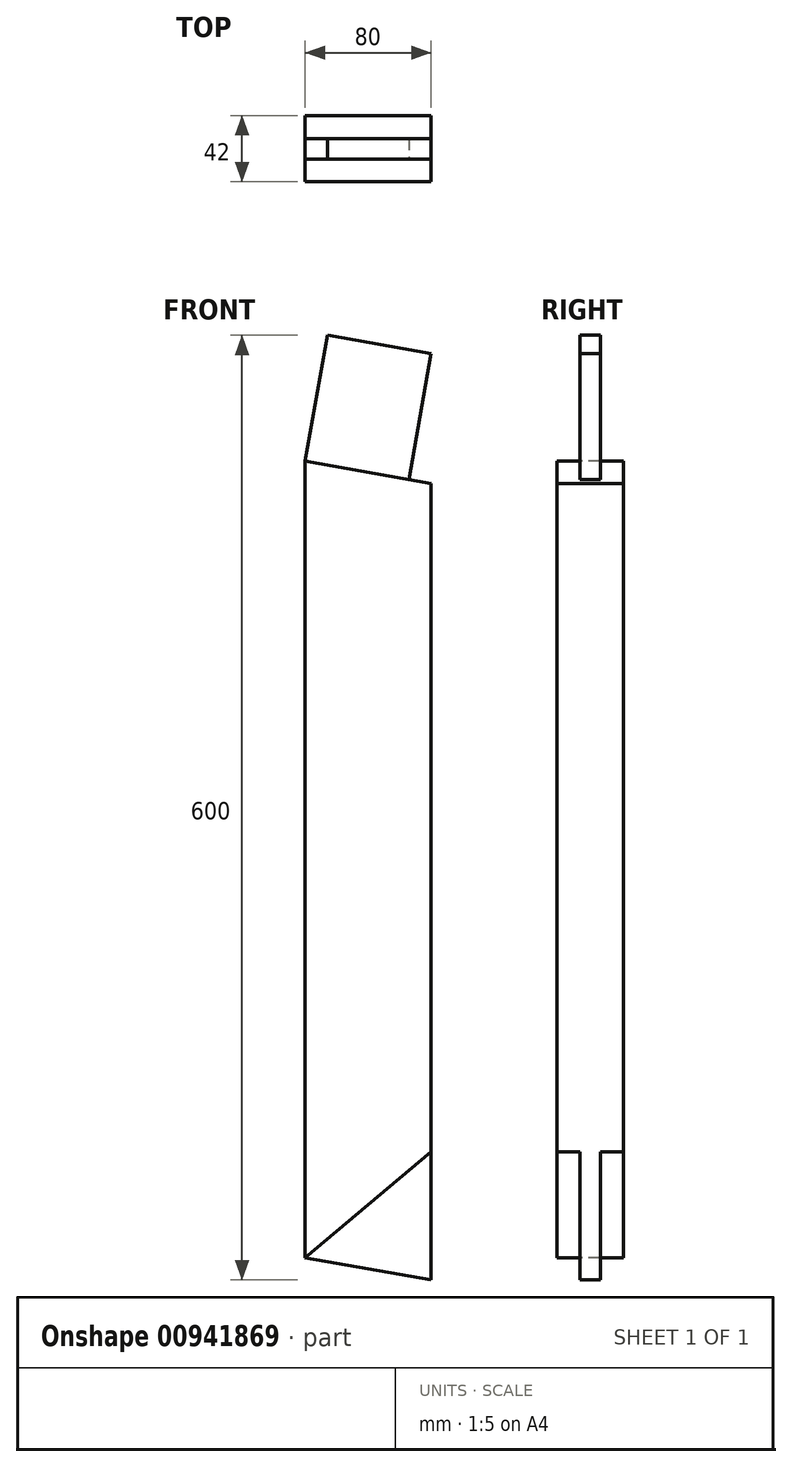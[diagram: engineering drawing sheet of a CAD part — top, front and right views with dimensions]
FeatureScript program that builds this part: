
annotation { "Feature Type Name" : "Feature", "Feature Type Description" : "" }
export const myFeature = defineFeature(function(context is Context, id is Id, definition is map)
    precondition{}
    {
        {
            var Q0;
            Q0=qCreatedBy(makeId("Front.planeOp"),FACE);
            var sketch = newSketch(context, id + "F0", { "sketchPlane" : qUnion([Q0])});
            skLineSegment(sketch, "E0.bottom", {"start": v(40, -300) * mm, "end": v(-40, -300) * mm});
            skLineSegment(sketch, "E0.top", {"start": v(40, 300) * mm, "end": v(-40, 300) * mm});
            skLineSegment(sketch, "E0.left", {"start": v(40, -300) * mm, "end": v(40, 300) * mm});
            skLineSegment(sketch, "E0.right", {"start": v(-40, -300) * mm, "end": v(-40, 300) * mm});
            skPoint(sketch, "E0.middle", {"position": v(0, 0) * mm});
            skSolve(sketch);
        }
        {
            var Q0;
            Q0=makeQuery(id+"F0.imprint","IMPRINT",FACE,{"disambiguationData":[TD([[makeQuery(id+"F0.imprint","IMPRINT",EDGE,{"derivedFrom":sQuery(id+"F0.wireOp",EDGE,"E0.bottom")}),-1.0]])]});
            extrude(context, id + "F1", {"entities" : qUnion([Q0]), "depth" : 42 * mm, "offsetDistance" : 25 * mm});
        }
        {
            var Q0;
            Q0=makeQuery(id+"F1.opExtrude","CAP_FACE",FACE,{"disambiguationData":[OSD([sQuery(id+"F0.wireOp",EDGE,"E0.bottom"),sQuery(id+"F0.wireOp",EDGE,"E0.top"),sQuery(id+"F0.wireOp",EDGE,"E0.left"),sQuery(id+"F0.wireOp",EDGE,"E0.right")])],"isStart":false});
            var sketch = newSketch(context, id + "F2", { "sketchPlane" : qUnion([Q0])});
            skLineSegment(sketch, "E1.bottom", {"start": v(-40, 300) * mm, "end": v(40, 300) * mm});
            skLineSegment(sketch, "E1.top", {"start": v(-40, 220) * mm, "end": v(40, 220) * mm});
            skLineSegment(sketch, "E1.left", {"start": v(-40, 300) * mm, "end": v(-40, 220) * mm});
            skLineSegment(sketch, "E1.right", {"start": v(40, 300) * mm, "end": v(40, 220) * mm});
            skSolve(sketch);
        }
        {
            var Q0;
            Q0=makeQuery(id+"F2.imprint","IMPRINT",FACE,{"disambiguationData":[TD([[makeQuery(id+"F2.imprint","IMPRINT",EDGE,{"derivedFrom":sQuery(id+"F2.wireOp",EDGE,"E1.bottom")}),1.0]])]});
            extrude(context, id + "F3", {"entities" : qUnion([Q0]), "operationType" : NewBodyOperationType.REMOVE, "oppositeDirection" : true, "depth" : 14.5 * mm, "offsetDistance" : 25 * mm});
        }
        {
            var Q0;
            Q0=makeQuery(id+"F1.opExtrude","CAP_FACE",FACE,{"disambiguationData":[OSD([sQuery(id+"F0.wireOp",EDGE,"E0.bottom"),sQuery(id+"F0.wireOp",EDGE,"E0.top"),sQuery(id+"F0.wireOp",EDGE,"E0.left"),sQuery(id+"F0.wireOp",EDGE,"E0.right")])],"isStart":true});
            var sketch = newSketch(context, id + "F4", { "sketchPlane" : qUnion([Q0])});
            skLineSegment(sketch, "E2.bottom", {"start": v(40, 300) * mm, "end": v(-40, 300) * mm});
            skLineSegment(sketch, "E2.top", {"start": v(40, 220) * mm, "end": v(-40, 220) * mm});
            skLineSegment(sketch, "E2.left", {"start": v(40, 300) * mm, "end": v(40, 220) * mm});
            skLineSegment(sketch, "E2.right", {"start": v(-40, 300) * mm, "end": v(-40, 220) * mm});
            skSolve(sketch);
        }
        {
            var Q0;
            Q0=makeQuery(id+"F4.imprint","IMPRINT",FACE,{"disambiguationData":[TD([[makeQuery(id+"F4.imprint","IMPRINT",EDGE,{"derivedFrom":sQuery(id+"F4.wireOp",EDGE,"E2.bottom")}),-1.0]])]});
            extrude(context, id + "F5", {"entities" : qUnion([Q0]), "operationType" : NewBodyOperationType.REMOVE, "oppositeDirection" : true, "depth" : 14.5 * mm, "offsetDistance" : 25 * mm});
        }
        {
            var Q0;
            Q0=makeQuery(id+"F1.opExtrude","CAP_FACE",FACE,{"disambiguationData":[OSD([sQuery(id+"F0.wireOp",EDGE,"E0.bottom"),sQuery(id+"F0.wireOp",EDGE,"E0.top"),sQuery(id+"F0.wireOp",EDGE,"E0.left"),sQuery(id+"F0.wireOp",EDGE,"E0.right")])],"isStart":false});
            var sketch = newSketch(context, id + "F6", { "sketchPlane" : qUnion([Q0])});
            skLineSegment(sketch, "E3", {"start": v(-40, 220) * mm, "end": v(40, 205.9) * mm});
            skLineSegment(sketch, "E4", {"start": v(40, 205.9) * mm, "end": v(40, 220) * mm});
            skLineSegment(sketch, "E5", {"start": v(40, 220) * mm, "end": v(-40, 220) * mm});
            skSolve(sketch);
        }
        {
            var Q0;
            Q0=makeQuery(id+"F6.imprint","IMPRINT",FACE,{"disambiguationData":[TD([[makeQuery(id+"F6.imprint","IMPRINT",EDGE,{"derivedFrom":sQuery(id+"F6.wireOp",EDGE,"E3")}),1.0]])]});
            var Q1;
            Q1=makeQuery(id+"F3.boolean.opBoolean","COPY",FACE,{"derivedFrom":makeQuery(id+"F3.opExtrude","CAP_FACE",FACE,{"disambiguationData":[OSD([sQuery(id+"F2.wireOp",EDGE,"E1.bottom"),sQuery(id+"F2.wireOp",EDGE,"E1.top"),sQuery(id+"F2.wireOp",EDGE,"E1.left"),sQuery(id+"F2.wireOp",EDGE,"E1.right")])],"isStart":false})});
            extrude(context, id + "F7", {"entities" : qUnion([Q0]), "operationType" : NewBodyOperationType.REMOVE, "endBound" : BoundingType.UP_TO_SURFACE, "oppositeDirection" : true, "depth" : 25 * mm, "endBoundEntityFace" : qUnion([Q1]), "offsetDistance" : 25 * mm});
        }
        {
            var Q0;
            Q0=makeQuery(id+"F1.opExtrude","CAP_FACE",FACE,{"disambiguationData":[OSD([sQuery(id+"F0.wireOp",EDGE,"E0.bottom"),sQuery(id+"F0.wireOp",EDGE,"E0.top"),sQuery(id+"F0.wireOp",EDGE,"E0.left"),sQuery(id+"F0.wireOp",EDGE,"E0.right")])],"isStart":true});
            var sketch = newSketch(context, id + "F8", { "sketchPlane" : qUnion([Q0])});
            skLineSegment(sketch, "E6", {"start": v(40, 220) * mm, "end": v(-40, 220) * mm});
            skLineSegment(sketch, "E7", {"start": v(-40, 220) * mm, "end": v(-40, 205.9) * mm});
            skLineSegment(sketch, "E8", {"start": v(-40, 205.9) * mm, "end": v(40, 220) * mm});
            skSolve(sketch);
        }
        {
            var Q0;
            Q0=makeQuery(id+"F8.imprint","IMPRINT",FACE,{"disambiguationData":[TD([[makeQuery(id+"F8.imprint","IMPRINT",EDGE,{"derivedFrom":sQuery(id+"F8.wireOp",EDGE,"E6")}),1.0]])]});
            var Q1;
            Q1=makeQuery(id+"F5.boolean.opBoolean","COPY",FACE,{"derivedFrom":makeQuery(id+"F5.opExtrude","CAP_FACE",FACE,{"disambiguationData":[OSD([sQuery(id+"F4.wireOp",EDGE,"E2.bottom"),sQuery(id+"F4.wireOp",EDGE,"E2.top"),sQuery(id+"F4.wireOp",EDGE,"E2.left"),sQuery(id+"F4.wireOp",EDGE,"E2.right")])],"isStart":false})});
            extrude(context, id + "F9", {"entities" : qUnion([Q0]), "operationType" : NewBodyOperationType.REMOVE, "endBound" : BoundingType.UP_TO_SURFACE, "oppositeDirection" : true, "depth" : 25 * mm, "endBoundEntityFace" : qUnion([Q1]), "offsetDistance" : 25 * mm});
        }
        {
            var Q0;
            Q0=makeQuery(id+"F7.boolean.opBoolean","MERGE",FACE,{"derivedFrom":[makeQuery(id+"F3.boolean.opBoolean","COPY",FACE,{"derivedFrom":makeQuery(id+"F3.opExtrude","CAP_FACE",FACE,{"disambiguationData":[OSD([sQuery(id+"F2.wireOp",EDGE,"E1.bottom"),sQuery(id+"F2.wireOp",EDGE,"E1.top"),sQuery(id+"F2.wireOp",EDGE,"E1.left"),sQuery(id+"F2.wireOp",EDGE,"E1.right")])],"isStart":false})})],"fromTools":[makeQuery(id+"F7.opExtrude","CAP_FACE",FACE,{"disambiguationData":[OSD([sQuery(id+"F6.wireOp",EDGE,"E3"),sQuery(id+"F6.wireOp",EDGE,"E4"),sQuery(id+"F6.wireOp",EDGE,"E5")])],"isStart":false})]});
            var sketch = newSketch(context, id + "F10", { "sketchPlane" : qUnion([Q0])});
            skLineSegment(sketch, "E9", {"start": v(-40, 220) * mm, "end": v(-25.9, 300) * mm});
            skLineSegment(sketch, "E10", {"start": v(-25.9, 300) * mm, "end": v(40, 288.38) * mm});
            skLineSegment(sketch, "E11", {"start": v(40, 288.38) * mm, "end": v(25.9, 208.38) * mm});
            skLineSegment(sketch, "E12", {"start": v(25.9, 208.38) * mm, "end": v(-40, 220) * mm});
            skSolve(sketch);
        }
        {
            var Q0;
            {var subQ0=sQuery(id+"F10.wireOp",EDGE,"E9");Q0=makeQuery(id+"F10.imprint","IMPRINT",FACE,{"disambiguationData":[TD([[makeQuery(id+"F10.imprint","IMPRINT",EDGE,{"derivedFrom":subQ0}),1.0]])]});}
            var Q1;
            {var subQ0=sQuery(id+"F10.wireOp",EDGE,"E10");Q1=makeQuery(id+"F10.imprint","IMPRINT",FACE,{"disambiguationData":[TD([[makeQuery(id+"F10.imprint","IMPRINT",EDGE,{"derivedFrom":subQ0}),1.0]])]});}
            var Q2;
            {var subQ0=sQuery(id+"F10.wireOp",EDGE,"E11");Q2=makeQuery(id+"F10.imprint","IMPRINT",FACE,{"disambiguationData":[TD([[makeQuery(id+"F10.imprint","IMPRINT",EDGE,{"derivedFrom":subQ0}),1.0]])]});}
            extrude(context, id + "F11", {"entities" : qUnion([Q0, Q1, Q2]), "operationType" : NewBodyOperationType.REMOVE, "endBound" : BoundingType.THROUGH_ALL, "oppositeDirection" : true, "depth" : 25 * mm, "offsetDistance" : 25 * mm});
        }
        {
            var Q0;
            Q0=makeQuery(id+"F1.opExtrude","CAP_FACE",FACE,{"disambiguationData":[OSD([sQuery(id+"F0.wireOp",EDGE,"E0.bottom"),sQuery(id+"F0.wireOp",EDGE,"E0.top"),sQuery(id+"F0.wireOp",EDGE,"E0.left"),sQuery(id+"F0.wireOp",EDGE,"E0.right")])],"isStart":false});
            var sketch = newSketch(context, id + "F12", { "sketchPlane" : qUnion([Q0])});
            skLineSegment(sketch, "E13", {"start": v(40, -300) * mm, "end": v(-40, -285.9) * mm});
            skLineSegment(sketch, "E14", {"start": v(-40, -285.9) * mm, "end": v(-40, -300) * mm});
            skLineSegment(sketch, "E15", {"start": v(-40, -300) * mm, "end": v(40, -300) * mm});
            skSolve(sketch);
        }
        {
            var Q0;
            Q0=makeQuery(id+"F12.imprint","IMPRINT",FACE,{"disambiguationData":[TD([[makeQuery(id+"F12.imprint","IMPRINT",EDGE,{"derivedFrom":sQuery(id+"F12.wireOp",EDGE,"E13")}),1.0]])]});
            extrude(context, id + "F13", {"entities" : qUnion([Q0]), "operationType" : NewBodyOperationType.REMOVE, "endBound" : BoundingType.THROUGH_ALL, "oppositeDirection" : true, "depth" : 16 * mm, "offsetDistance" : 25 * mm});
        }
        {
            var Q0;
            Q0=makeQuery(id+"F1.opExtrude","CAP_FACE",FACE,{"disambiguationData":[OSD([sQuery(id+"F0.wireOp",EDGE,"E0.bottom"),sQuery(id+"F0.wireOp",EDGE,"E0.top"),sQuery(id+"F0.wireOp",EDGE,"E0.left"),sQuery(id+"F0.wireOp",EDGE,"E0.right")])],"isStart":false});
            var sketch = newSketch(context, id + "F14", { "sketchPlane" : qUnion([Q0])});
            skLineSegment(sketch, "E16", {"start": v(40, -300) * mm, "end": v(40, -218.77) * mm});
            skLineSegment(sketch, "E17", {"start": v(40, -218.77) * mm, "end": v(-40, -285.9) * mm});
            skLineSegment(sketch, "E18", {"start": v(-40, -285.9) * mm, "end": v(40, -300) * mm});
            skSolve(sketch);
        }
        {
            var Q0;
            Q0=makeQuery(id+"F14.imprint","IMPRINT",FACE,{"disambiguationData":[TD([[makeQuery(id+"F14.imprint","IMPRINT",EDGE,{"derivedFrom":sQuery(id+"F14.wireOp",EDGE,"E16")}),1.0]])]});
            extrude(context, id + "F15", {"entities" : qUnion([Q0]), "operationType" : NewBodyOperationType.REMOVE, "oppositeDirection" : true, "depth" : 14.5 * mm, "offsetDistance" : 25 * mm});
        }
        {
            var Q0;
            Q0=makeQuery(id+"F1.opExtrude","CAP_FACE",FACE,{"disambiguationData":[OSD([sQuery(id+"F0.wireOp",EDGE,"E0.bottom"),sQuery(id+"F0.wireOp",EDGE,"E0.top"),sQuery(id+"F0.wireOp",EDGE,"E0.left"),sQuery(id+"F0.wireOp",EDGE,"E0.right")])],"isStart":true});
            var sketch = newSketch(context, id + "F16", { "sketchPlane" : qUnion([Q0])});
            skLineSegment(sketch, "E19", {"start": v(-40, -300) * mm, "end": v(40, -285.9) * mm});
            skLineSegment(sketch, "E20", {"start": v(40, -285.9) * mm, "end": v(-40, -218.77) * mm});
            skLineSegment(sketch, "E21", {"start": v(-40, -218.77) * mm, "end": v(-40, -300) * mm});
            skSolve(sketch);
        }
        {
            var Q0;
            Q0=makeQuery(id+"F16.imprint","IMPRINT",FACE,{"disambiguationData":[TD([[makeQuery(id+"F16.imprint","IMPRINT",EDGE,{"derivedFrom":sQuery(id+"F16.wireOp",EDGE,"E19")}),1.0]])]});
            extrude(context, id + "F17", {"entities" : qUnion([Q0]), "operationType" : NewBodyOperationType.REMOVE, "oppositeDirection" : true, "depth" : 14.5 * mm, "offsetDistance" : 25 * mm});
        }
    });
